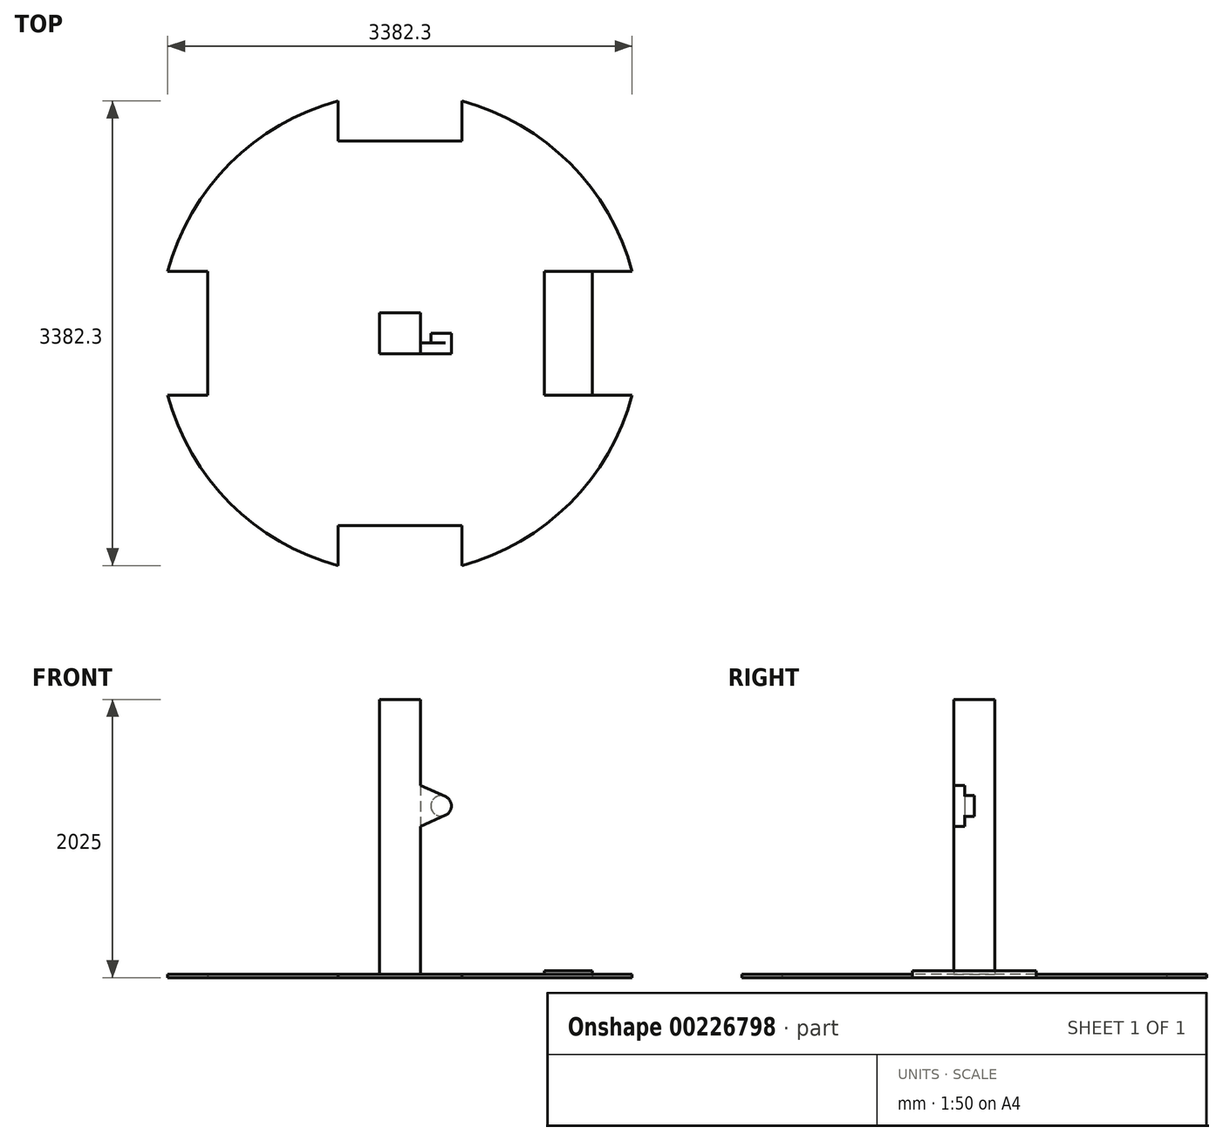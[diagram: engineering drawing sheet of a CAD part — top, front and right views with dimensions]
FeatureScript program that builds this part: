
annotation { "Feature Type Name" : "Feature", "Feature Type Description" : "" }
export const myFeature = defineFeature(function(context is Context, id is Id, definition is map)
    precondition{}
    {
        {
            var Q0;
            Q0=qCreatedBy(makeId("Top.planeOp"),FACE);
            var sketch = newSketch(context, id + "F0", { "sketchPlane" : qUnion([Q0])});
            skCircle(sketch, "E0", {"center": v(0, 0) * mm, "radius": 1800 * mm, "construction": true});
            skSolve(sketch);
        }
        {
            var Q0;
            Q0=qCreatedBy(makeId("Top.planeOp"),FACE);
            var sketch = newSketch(context, id + "F1", { "sketchPlane" : qUnion([Q0])});
            skLineSegment(sketch, "E1.bottom", {"start": v(450, -1400) * mm, "end": v(-450, -1400) * mm});
            skLineSegment(sketch, "E1.top", {"start": v(450, 1400) * mm, "end": v(-450, 1400) * mm});
            skLineSegment(sketch, "E1.left", {"start": v(450, -1691.15) * mm, "end": v(450, 1691.15) * mm});
            skLineSegment(sketch, "E1.right", {"start": v(-450, -1691.15) * mm, "end": v(-450, 1691.15) * mm});
            skPoint(sketch, "E1.middle", {"position": v(0, 0) * mm});
            skLineSegment(sketch, "E2.bottom", {"start": v(1691.15, -450) * mm, "end": v(-1691.15, -450) * mm});
            skLineSegment(sketch, "E2.top", {"start": v(1691.15, 450) * mm, "end": v(-1691.15, 450) * mm});
            skLineSegment(sketch, "E2.left", {"start": v(1400, -450) * mm, "end": v(1400, 450) * mm});
            skLineSegment(sketch, "E2.right", {"start": v(-1400, -450) * mm, "end": v(-1400, 450) * mm});
            skCircle(sketch, "E3", {"center": v(0, 0) * mm, "radius": 1750 * mm});
            skSolve(sketch);
        }
        {
            var Q0;
            {var subQ2=sQuery(id+"F1.wireOp",EDGE,"E1.left");var subQ6=makeQuery(id+"F1.imprint","INTERSECT",VERTEX,{"derivedFrom":[sQuery(id+"F1.wireOp",EDGE,"E1.bottom"),subQ2]});Q0=makeQuery(id+"F1.imprint","IMPRINT",FACE,{"disambiguationData":[TD([[makeQuery(id+"F1.imprint","IMPRINT",EDGE,{"disambiguationData":[TD([[subQ6,1.0]])],"derivedFrom":subQ2}),-1.0]])]});}
            var Q1;
            {var subQ4=sQuery(id+"F1.wireOp",EDGE,"E1.left");var subQ5=makeQuery(id+"F1.imprint","INTERSECT",VERTEX,{"derivedFrom":[sQuery(id+"F1.wireOp",EDGE,"E1.top"),subQ4]});Q1=makeQuery(id+"F1.imprint","IMPRINT",FACE,{"disambiguationData":[TD([[makeQuery(id+"F1.imprint","IMPRINT",EDGE,{"disambiguationData":[TD([[subQ5,1.0]])],"derivedFrom":subQ4}),-1.0]])]});}
            var Q2;
            {var subQ2=sQuery(id+"F1.wireOp",EDGE,"E1.right");var subQ4=makeQuery(id+"F1.imprint","INTERSECT",VERTEX,{"derivedFrom":[sQuery(id+"F1.wireOp",EDGE,"E1.bottom"),subQ2]});Q2=makeQuery(id+"F1.imprint","IMPRINT",FACE,{"disambiguationData":[TD([[makeQuery(id+"F1.imprint","IMPRINT",EDGE,{"disambiguationData":[TD([[subQ4,1.0]])],"derivedFrom":subQ2}),1.0]])]});}
            var Q3;
            {var subQ2=sQuery(id+"F1.wireOp",EDGE,"E1.right");var subQ4=makeQuery(id+"F1.imprint","INTERSECT",VERTEX,{"derivedFrom":[sQuery(id+"F1.wireOp",EDGE,"E1.top"),subQ2]});Q3=makeQuery(id+"F1.imprint","IMPRINT",FACE,{"disambiguationData":[TD([[makeQuery(id+"F1.imprint","IMPRINT",EDGE,{"disambiguationData":[TD([[subQ4,1.0]])],"derivedFrom":subQ2}),1.0]])]});}
            var Q4;
            {var subQ0=sQuery(id+"F1.wireOp",EDGE,"E2.bottom");var subQ1=sQuery(id+"F1.wireOp",EDGE,"E1.left");var subQ2=makeQuery(id+"F1.imprint","INTERSECT",VERTEX,{"derivedFrom":[subQ1,subQ0]});Q4=makeQuery(id+"F1.imprint","IMPRINT",FACE,{"disambiguationData":[TD([[makeQuery(id+"F1.imprint","IMPRINT",EDGE,{"disambiguationData":[TD([[subQ2,-1.0]])],"derivedFrom":subQ1}),1.0]])]});}
            var Q5;
            {var subQ5=sQuery(id+"F1.wireOp",EDGE,"E2.right");Q5=makeQuery(id+"F1.imprint","IMPRINT",FACE,{"disambiguationData":[TD([[makeQuery(id+"F1.imprint","IMPRINT",EDGE,{"derivedFrom":subQ5}),-1.0]])]});}
            var Q6;
            {var subQ0=sQuery(id+"F1.wireOp",EDGE,"E1.top");Q6=makeQuery(id+"F1.imprint","IMPRINT",FACE,{"disambiguationData":[TD([[makeQuery(id+"F1.imprint","IMPRINT",EDGE,{"derivedFrom":subQ0}),1.0]])]});}
            var Q7;
            {var subQ5=sQuery(id+"F1.wireOp",EDGE,"E2.left");Q7=makeQuery(id+"F1.imprint","IMPRINT",FACE,{"disambiguationData":[TD([[makeQuery(id+"F1.imprint","IMPRINT",EDGE,{"derivedFrom":subQ5}),1.0]])]});}
            var Q8;
            {var subQ0=sQuery(id+"F1.wireOp",EDGE,"E1.bottom");Q8=makeQuery(id+"F1.imprint","IMPRINT",FACE,{"disambiguationData":[TD([[makeQuery(id+"F1.imprint","IMPRINT",EDGE,{"derivedFrom":subQ0}),-1.0]])]});}
            extrude(context, id + "F2", {"entities" : qUnion([Q0, Q1, Q2, Q3, Q4, Q5, Q6, Q7, Q8]), "depth" : 25 * mm});
        }
        {
            var Q0;
            Q0=makeQuery(id+"F2.opExtrude","CAP_FACE",FACE,{"disambiguationData":[OSD([sQuery(id+"F1.wireOp",EDGE,"E1.bottom"),sQuery(id+"F1.wireOp",EDGE,"E1.top"),sQuery(id+"F1.wireOp",EDGE,"E1.left"),sQuery(id+"F1.wireOp",EDGE,"E1.right"),sQuery(id+"F1.wireOp",EDGE,"E2.bottom"),sQuery(id+"F1.wireOp",EDGE,"E2.top"),sQuery(id+"F1.wireOp",EDGE,"E2.left"),sQuery(id+"F1.wireOp",EDGE,"E2.right"),sQuery(id+"F1.wireOp",EDGE,"E3")])],"isStart":false});
            var sketch = newSketch(context, id + "F3", { "sketchPlane" : qUnion([Q0])});
            skLineSegment(sketch, "E4.bottom", {"start": v(1400, 450) * mm, "end": v(1050, 450) * mm});
            skLineSegment(sketch, "E4.top", {"start": v(1400, -450) * mm, "end": v(1050, -450) * mm});
            skLineSegment(sketch, "E4.left", {"start": v(1400, 450) * mm, "end": v(1400, -450) * mm});
            skLineSegment(sketch, "E4.right", {"start": v(1050, 450) * mm, "end": v(1050, -450) * mm});
            skSolve(sketch);
        }
        {
            var Q0;
            {var subQ5=sQuery(id+"F3.wireOp",EDGE,"E4.left");Q0=makeQuery(id+"F3.imprint","IMPRINT",FACE,{"disambiguationData":[TD([[makeQuery(id+"F3.imprint","IMPRINT",EDGE,{"derivedFrom":subQ5}),1.0]])]});}
            extrude(context, id + "F4", {"entities" : qUnion([Q0]), "operationType" : NewBodyOperationType.ADD, "depth" : 25 * mm});
        }
        {
            var Q0;
            Q0=makeQuery(id+"F2.opExtrude","CAP_FACE",FACE,{"disambiguationData":[OSD([sQuery(id+"F1.wireOp",EDGE,"E1.bottom"),sQuery(id+"F1.wireOp",EDGE,"E1.top"),sQuery(id+"F1.wireOp",EDGE,"E1.left"),sQuery(id+"F1.wireOp",EDGE,"E1.right"),sQuery(id+"F1.wireOp",EDGE,"E2.bottom"),sQuery(id+"F1.wireOp",EDGE,"E2.top"),sQuery(id+"F1.wireOp",EDGE,"E2.left"),sQuery(id+"F1.wireOp",EDGE,"E2.right"),sQuery(id+"F1.wireOp",EDGE,"E3")])],"isStart":false});
            var sketch = newSketch(context, id + "F5", { "sketchPlane" : qUnion([Q0])});
            skLineSegment(sketch, "E5.bottom", {"start": v(150, -150) * mm, "end": v(-150, -150) * mm});
            skLineSegment(sketch, "E5.top", {"start": v(150, 150) * mm, "end": v(-150, 150) * mm});
            skLineSegment(sketch, "E5.left", {"start": v(150, -150) * mm, "end": v(150, 150) * mm});
            skLineSegment(sketch, "E5.right", {"start": v(-150, -150) * mm, "end": v(-150, 150) * mm});
            skPoint(sketch, "E5.middle", {"position": v(0, 0) * mm});
            skSolve(sketch);
        }
        {
            var Q0;
            Q0 = qSketchRegion(id + "F5", true);
            extrude(context, id + "F6", {"entities" : qUnion([Q0]), "operationType" : NewBodyOperationType.ADD, "depth" : 2000 * mm});
        }
        {
            var Q0;
            Q0=makeQuery(id+"F6.opExtrude","SWEPT_FACE",FACE,{"disambiguationData":[OSD([sQuery(id+"F5.wireOp",EDGE,"E5.bottom")])]});
            var sketch = newSketch(context, id + "F7", { "sketchPlane" : qUnion([Q0])});
            skLineSegment(sketch, "E6", {"start": v(150, 1400) * mm, "end": v(330.86, 1318.36) * mm});
            skLineSegment(sketch, "E7", {"start": v(150, 1400) * mm, "end": v(150, 1100) * mm});
            skLineSegment(sketch, "E8", {"start": v(150, 1100) * mm, "end": v(330.86, 1181.64) * mm});
            skArc(sketch, "E9", {"start": v(330.86, 1318.36) * mm, "mid": v(225, 1250) * mm, "end": v(330.86, 1181.64) * mm});
            skArc(sketch, "E10", {"start": v(330.86, 1181.64) * mm, "mid": v(375, 1250) * mm, "end": v(330.86, 1318.36) * mm});
            skSolve(sketch);
        }
        {
            var Q0;
            Q0=makeQuery(id+"F7.imprint","IMPRINT",FACE,{"disambiguationData":[TD([[makeQuery(id+"F7.imprint","IMPRINT",EDGE,{"derivedFrom":sQuery(id+"F7.wireOp",EDGE,"E6")}),-1.0]])]});
            var Q1;
            Q1=makeQuery(id+"F7.imprint","IMPRINT",FACE,{"disambiguationData":[TD([[makeQuery(id+"F7.imprint","IMPRINT",EDGE,{"derivedFrom":sQuery(id+"F7.wireOp",EDGE,"E9")}),1.0]])]});
            extrude(context, id + "F8", {"entities" : qUnion([Q0, Q1]), "operationType" : NewBodyOperationType.ADD, "oppositeDirection" : true, "depth" : 80 * mm});
        }
        {
            var Q0;
            Q0=makeQuery(id+"F7.imprint","IMPRINT",FACE,{"disambiguationData":[TD([[makeQuery(id+"F7.imprint","IMPRINT",EDGE,{"derivedFrom":sQuery(id+"F7.wireOp",EDGE,"E9")}),1.0]])]});
            extrude(context, id + "F9", {"entities" : qUnion([Q0]), "operationType" : NewBodyOperationType.ADD, "oppositeDirection" : true, "depth" : 150 * mm});
        }
    });
